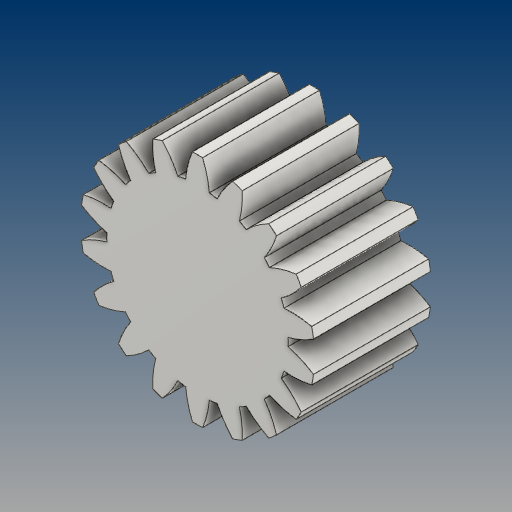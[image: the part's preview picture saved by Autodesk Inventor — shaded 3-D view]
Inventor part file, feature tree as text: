
AUTODESK INVENTOR PART (.ipt)
format: ipt  version: 2021 (Build 250183000, 183)  size: 262,144 bytes
history: native  units: mm (DEFAULTED — no unit token found)
features: plane x3, other x3, sketch x2, extrude x1
ambient origin geometry x8: Origin, YZ Plane, XZ Plane, XY Plane, X Axis, Y Axis, Z Axis, Center Point
bodies: Solid1 (feature_tree)
feature tree (9):
  extrude  "Extrusion1"  Depth=20.0mm TaperAngle=0.0deg
  plane  "Work Plane2"
  plane  "Work Plane8"
  plane  "Work Plane9"
  other  "Spur Gear"
  sketch  "Sketch1"  dims[d0=40.0mm d1=20.0mm d2=0.0mm]
  sketch  "Sketch2"  dims[d3=36.0mm d4=10.0mm d5=0.0mm d16=90.0mm d17=0.0mm d34=1.745329mm d39=0.0mm d41=0.0mm d43=90.0mm d46=90.0mm d47=0.0mm d48=0.0mm]
  other  "Srf1"
  other  "Pitch Diameter"
